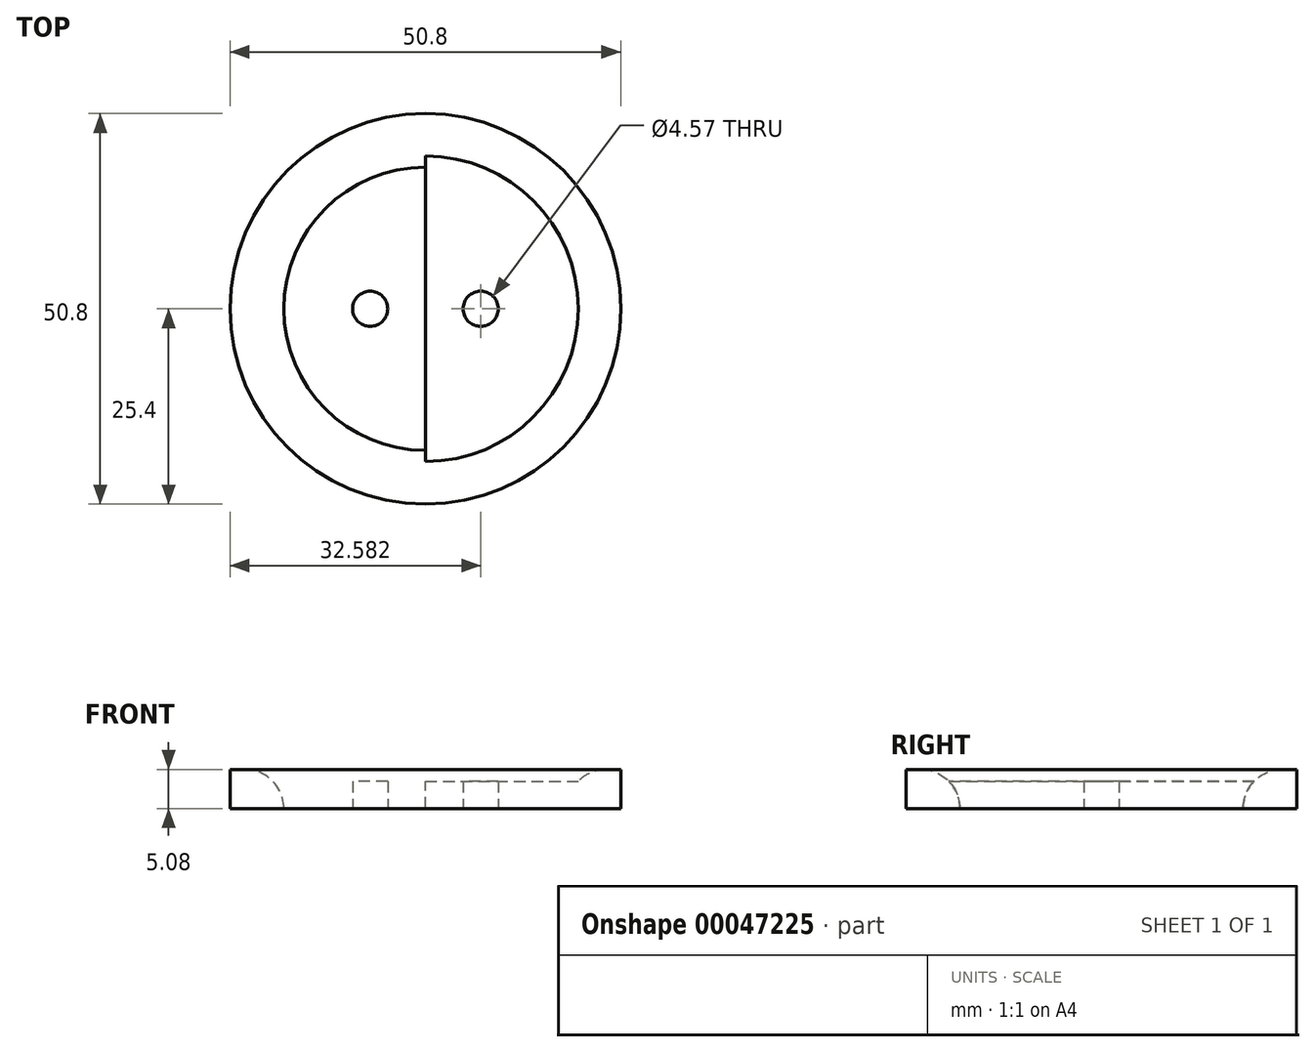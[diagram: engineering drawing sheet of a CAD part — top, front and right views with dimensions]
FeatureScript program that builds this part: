
annotation { "Feature Type Name" : "Feature", "Feature Type Description" : "" }
export const myFeature = defineFeature(function(context is Context, id is Id, definition is map)
    precondition{}
    {
        {
            var Q0;
            Q0=qCreatedBy(makeId("Top.planeOp"),FACE);
            var sketch = newSketch(context, id + "F0", { "sketchPlane" : qUnion([Q0])});
            skCircle(sketch, "E0", {"center": v(0, 0) * mm, "radius": 25.4 * mm});
            skCircle(sketch, "E1", {"center": v(0, 0) * mm, "radius": 18.41 * mm});
            skLineSegment(sketch, "E2", {"start": v(0, 38.11) * mm, "end": v(0, -48.24) * mm});
            skCircle(sketch, "E3", {"center": v(7.18, 0) * mm, "radius": 2.29 * mm});
            skCircle(sketch, "E4.MirrorC", {"center": v(-7.18, 0) * mm, "radius": 2.29 * mm});
            skSolve(sketch);
        }
        {
            var Q0;
            Q0 = qSketchRegion(id + "F0", true);
            extrude(context, id + "F1", {"entities" : qUnion([Q0]), "depth" : 5.08 * mm});
        }
        {
            var Q0;
            Q0=makeQuery(id+"F0.imprint","IMPRINT",FACE,{"disambiguationData":[TD([[makeQuery(id+"F0.imprint","IMPRINT",EDGE,{"derivedFrom":sQuery(id+"F0.wireOp",EDGE,"E4.MirrorC")}),1.0]])]});
            var Q1;
            Q1=makeQuery(id+"F0.imprint","IMPRINT",FACE,{"disambiguationData":[TD([[makeQuery(id+"F0.imprint","IMPRINT",EDGE,{"derivedFrom":sQuery(id+"F0.wireOp",EDGE,"E3")}),-1.0]])]});
            extrude(context, id + "F2", {"entities" : qUnion([Q0, Q1]), "operationType" : NewBodyOperationType.ADD, "depth" : 3.56 * mm});
        }
        {
            var Q0;
            Q0=makeQuery(id+"F1.opExtrude","CAP_EDGE",EDGE,{"disambiguationData":[OSD([sQuery(id+"F0.wireOp",EDGE,"E1")])],"isStart":false});
            fillet(context, id + "F3", {"entities" : qUnion([Q0]), "radius" : 5.08 * mm, "tangentPropagation" : true, "allowEdgeOverflow" : false});
        }
    });
